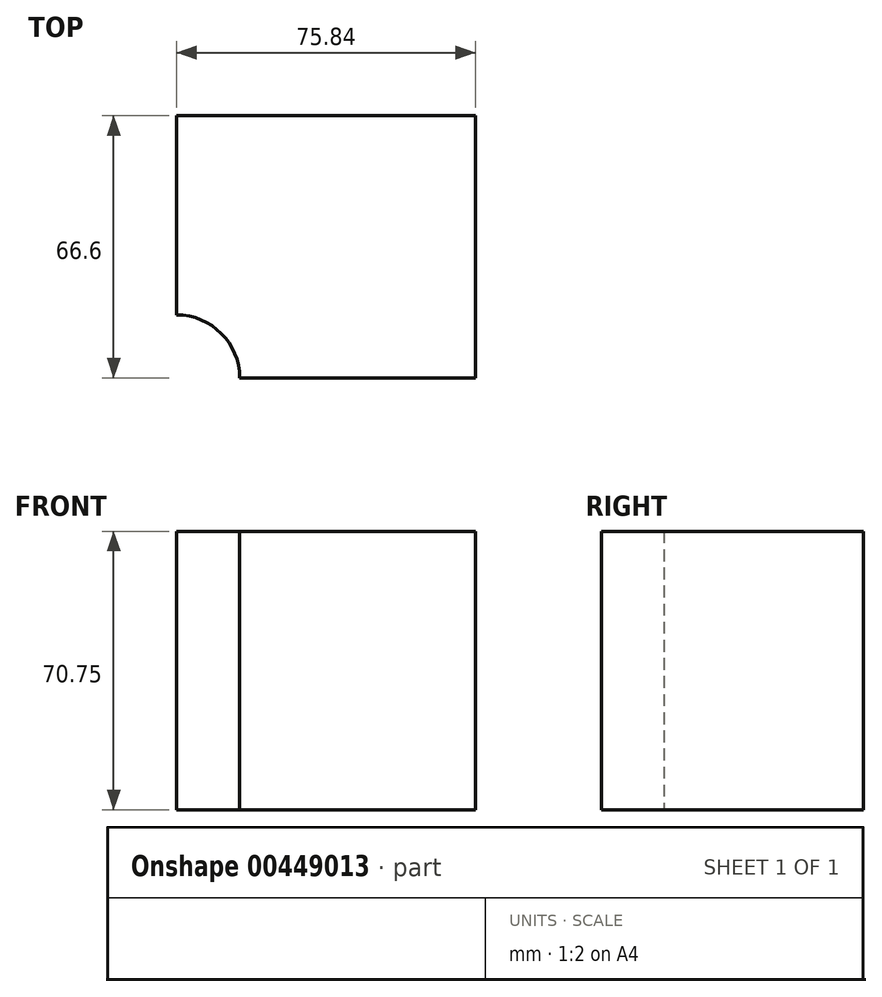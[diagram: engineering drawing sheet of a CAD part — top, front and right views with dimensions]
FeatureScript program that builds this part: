
annotation { "Feature Type Name" : "Feature", "Feature Type Description" : "" }
export const myFeature = defineFeature(function(context is Context, id is Id, definition is map)
    precondition{}
    {
        {
            var Q0;
            Q0=qCreatedBy(makeId("Top.planeOp"),FACE);
            var sketch = newSketch(context, id + "F0", { "sketchPlane" : qUnion([Q0])});
            skLineSegment(sketch, "E0.bottom", {"start": v(-37.92, 33.3) * mm, "end": v(37.92, 33.3) * mm});
            skLineSegment(sketch, "E0.top", {"start": v(-37.92, -33.3) * mm, "end": v(37.92, -33.3) * mm});
            skLineSegment(sketch, "E0.left", {"start": v(-37.92, 33.3) * mm, "end": v(-37.92, -33.3) * mm});
            skLineSegment(sketch, "E0.right", {"start": v(37.92, 33.3) * mm, "end": v(37.92, -33.3) * mm});
            skPoint(sketch, "E0.middle", {"position": v(0, 0) * mm});
            skCircle(sketch, "E1", {"center": v(-37.92, -33.3) * mm, "radius": 15.98 * mm});
            skLineSegment(sketch, "E2.bottom", {"start": v(37.92, -14.87) * mm, "end": v(89.9, -14.87) * mm});
            skLineSegment(sketch, "E2.top", {"start": v(37.92, 17) * mm, "end": v(89.9, 17) * mm});
            skLineSegment(sketch, "E2.left", {"start": v(37.92, -14.87) * mm, "end": v(37.92, 17) * mm});
            skLineSegment(sketch, "E2.right", {"start": v(89.9, -14.87) * mm, "end": v(89.9, 17) * mm});
            skSolve(sketch);
        }
        {
            var Q0;
            Q0=qCreatedBy(makeId("Front.planeOp"),FACE);
            var sketch = newSketch(context, id + "F1", { "sketchPlane" : qUnion([Q0])});
            skPoint(sketch, "E3", {"position": v(59.3, 75) * mm});
            skLineSegment(sketch, "E4", {"start": v(59.3, 75) * mm, "end": v(52.06, 75) * mm, "construction": true});
            skLineSegment(sketch, "E5", {"start": v(52.06, 75) * mm, "end": v(52.06, 70.75) * mm, "construction": true});
            skLineSegment(sketch, "E6", {"start": v(52.06, 70.75) * mm, "end": v(56.13, 70.75) * mm, "construction": true});
            skLineSegment(sketch, "E7", {"start": v(56.13, 70.75) * mm, "end": v(56.13, 58.04) * mm, "construction": true});
            skLineSegment(sketch, "E8", {"start": v(56.13, 58.04) * mm, "end": v(59.3, 58.04) * mm, "construction": true});
            skLineSegment(sketch, "E9", {"start": v(59.3, 58.04) * mm, "end": v(59.3, 75) * mm, "construction": true});
            skSolve(sketch);
        }
        {
            var Q0;
            {var subQ3=sQuery(id+"F0.wireOp",EDGE,"weMGhbSe-tSFA-Np6Z-37OD-lU2MjtnzNAk4");Q0=makeQuery(id+"F0.imprint","IMPRINT",FACE,{"disambiguationData":[TD([[makeQuery(id+"F0.imprint","IMPRINT",EDGE,{"derivedFrom":subQ3}),-1.0]])]});}
            var Q1;
            {var subQ1=sQuery(id+"F0.wireOp",EDGE,"E0.bottom");Q1=makeQuery(id+"F0.imprint","IMPRINT",FACE,{"disambiguationData":[TD([[makeQuery(id+"F0.imprint","IMPRINT",EDGE,{"derivedFrom":subQ1}),-1.0]])]});}
            var Q2;
            Q2=sQuery(id+"F1.wireOp",VERTEX,"E7.start");
            extrude(context, id + "F2", {"entities" : qUnion([Q0, Q1]), "endBound" : BoundingType.UP_TO_VERTEX, "endBoundEntityVertex" : qUnion([Q2]), "depth" : 25 * mm});
        }
    });
